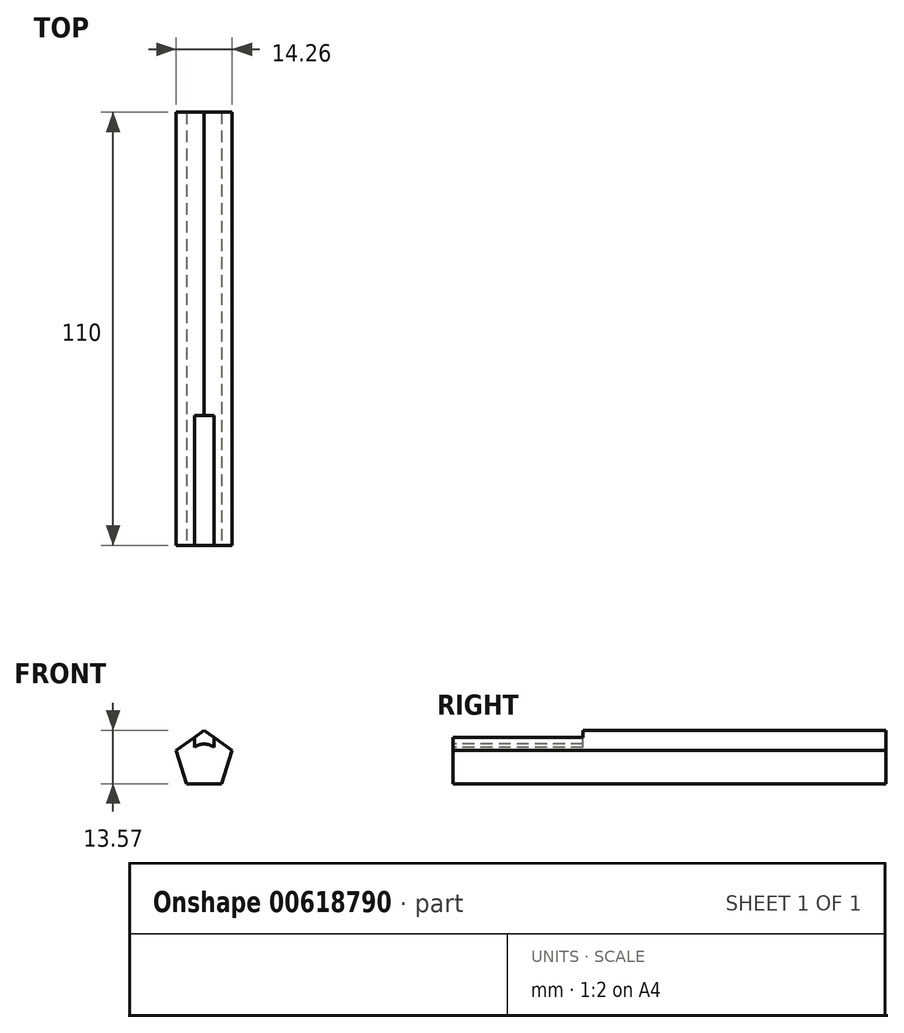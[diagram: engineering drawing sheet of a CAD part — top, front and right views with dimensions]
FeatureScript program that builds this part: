
annotation { "Feature Type Name" : "Feature", "Feature Type Description" : "" }
export const myFeature = defineFeature(function(context is Context, id is Id, definition is map)
    precondition{}
    {
        {
            var Q0;
            Q0=qCreatedBy(makeId("Front.planeOp"),FACE);
            var sketch = newSketch(context, id + "F0", { "sketchPlane" : qUnion([Q0])});
            skCircle(sketch, "E0", {"center": v(0, 0) * mm, "radius": 7.5 * mm});
            skCircle(sketch, "E1", {"center": v(0, 0) * mm, "radius": 1.5 * mm});
            skCircle(sketch, "E2", {"center": v(0, 0) * mm, "radius": 4 * mm});
            skCircle(sketch, "E3", {"center": v(0, 0) * mm, "radius": 5 * mm});
            skCircle(sketch, "E4.cCircle", {"center": v(0, 0) * mm, "radius": 7.5 * mm, "construction": true});
            skLineSegment(sketch, "E4.0", {"start": v(4.4, -6.07) * mm, "end": v(-4.4, -6.07) * mm});
            skLineSegment(sketch, "E4.1", {"start": v(-4.4, -6.07) * mm, "end": v(-7.13, 2.32) * mm});
            skLineSegment(sketch, "E4.2", {"start": v(-7.13, 2.32) * mm, "end": v(0, 7.5) * mm});
            skLineSegment(sketch, "E4.3", {"start": v(0, 7.5) * mm, "end": v(7.13, 2.32) * mm});
            skLineSegment(sketch, "E4.4", {"start": v(7.13, 2.32) * mm, "end": v(4.4, -6.07) * mm});
            skSolve(sketch);
        }
        {
            var Q0;
            Q0=qCreatedBy(makeId("Right.planeOp"),FACE);
            var sketch = newSketch(context, id + "F1", { "sketchPlane" : qUnion([Q0])});
            skLineSegment(sketch, "E5", {"start": v(0, 0) * mm, "end": v(95, 0) * mm});
            skLineSegment(sketch, "E6", {"start": v(0, 0) * mm, "end": v(0, 5.5) * mm});
            skLineSegment(sketch, "E7", {"start": v(0, 5.5) * mm, "end": v(95, 5.5) * mm});
            skLineSegment(sketch, "E8", {"start": v(95, 0) * mm, "end": v(110, 0) * mm});
            skLineSegment(sketch, "E9", {"start": v(0, 0) * mm, "end": v(0, 4) * mm});
            skLineSegment(sketch, "E10", {"start": v(0, 4) * mm, "end": v(95, 4) * mm});
            skLineSegment(sketch, "E11", {"start": v(95, 4) * mm, "end": v(110, 1.5) * mm});
            skLineSegment(sketch, "E12", {"start": v(110, 1.5) * mm, "end": v(110, 0) * mm});
            skLineSegment(sketch, "E13", {"start": v(95, 5.5) * mm, "end": v(110, 5.5) * mm});
            skLineSegment(sketch, "E14", {"start": v(110, 5.5) * mm, "end": v(110, 1.5) * mm});
            skSolve(sketch);
        }
        {
            var Q0;
            Q0=makeQuery(id+"F1.imprint","IMPRINT",FACE,{"disambiguationData":[TD([[makeQuery(id+"F1.imprint","IMPRINT",EDGE,{"derivedFrom":sQuery(id+"F1.wireOp",EDGE,"E6")}),-1.0]])]});
            var Q1;
            Q1=sQuery(id+"F1.wireOp",EDGE,"E5");
            revolve(context, id + "F2", {"entities" : qUnion([Q0]), "axis" : qUnion([Q1]), "revolveType" : RevolveType.FULL});
        }
        {
            var Q0;
            Q0=makeQuery(id+"F0.imprint","IMPRINT",FACE,{"disambiguationData":[TD([[makeQuery(id+"F0.imprint","IMPRINT",EDGE,{"derivedFrom":sQuery(id+"F0.wireOp",EDGE,"E3")}),-1.0]])]});
            extrude(context, id + "F3", {"entities" : qUnion([Q0]), "operationType" : NewBodyOperationType.ADD, "oppositeDirection" : true, "depth" : 110 * mm, "offsetDistance" : 25 * mm});
        }
        {
            var Q0;
            Q0=makeQuery(id+"F3.boolean.opBoolean","MERGE",FACE,{"derivedFrom":[makeQuery(id+"F2.opRevolve","SWEPT_FACE",FACE,{"disambiguationData":[OSD([sQuery(id+"F1.wireOp",EDGE,"E6")])]}),makeQuery(id+"F3.opExtrude","CAP_FACE",FACE,{"disambiguationData":[OSD([sQuery(id+"F0.wireOp",EDGE,"E3"),sQuery(id+"F0.wireOp",EDGE,"E4.0"),sQuery(id+"F0.wireOp",EDGE,"E4.1"),sQuery(id+"F0.wireOp",EDGE,"E4.2"),sQuery(id+"F0.wireOp",EDGE,"E4.3"),sQuery(id+"F0.wireOp",EDGE,"E4.4")])],"isStart":true})]});
            var sketch = newSketch(context, id + "F4", { "sketchPlane" : qUnion([Q0])});
            skCircle(sketch, "E15", {"center": v(0, 0) * mm, "radius": 4 * mm});
            skLineSegment(sketch, "E16", {"start": v(0, 0) * mm, "end": v(4, 0) * mm});
            skLineSegment(sketch, "E17", {"start": v(0, 0) * mm, "end": v(0, 10) * mm});
            skLineSegment(sketch, "E18", {"start": v(2.5, 0) * mm, "end": v(2.5, 10) * mm});
            skLineSegment(sketch, "E19", {"start": v(-2.5, 0) * mm, "end": v(-2.5, 10) * mm});
            skLineSegment(sketch, "E20", {"start": v(-2.5, 0) * mm, "end": v(0, 0) * mm});
            skLineSegment(sketch, "E21", {"start": v(-2.5, 10) * mm, "end": v(0, 10) * mm});
            skLineSegment(sketch, "E22", {"start": v(2.5, 10) * mm, "end": v(0, 10) * mm});
            skSolve(sketch);
        }
        {
            var Q0;
            {var subQ0=sQuery(id+"F4.wireOp",EDGE,"E17");var subQ1=sQuery(id+"F4.wireOp",EDGE,"E15");var subQ2=makeQuery(id+"F4.imprint","INTERSECT",VERTEX,{"derivedFrom":[subQ1,subQ0]});Q0=makeQuery(id+"F4.imprint","IMPRINT",FACE,{"disambiguationData":[TD([[makeQuery(id+"F4.imprint","IMPRINT",EDGE,{"disambiguationData":[TD([[subQ2,-1.0]])],"derivedFrom":subQ1}),-1.0]])]});}
            var Q1;
            {var subQ0=sQuery(id+"F4.wireOp",EDGE,"E18");var subQ1=sQuery(id+"F4.wireOp",EDGE,"E15");var subQ2=makeQuery(id+"F4.imprint","INTERSECT",VERTEX,{"derivedFrom":[subQ1,subQ0]});Q1=makeQuery(id+"F4.imprint","IMPRINT",FACE,{"disambiguationData":[TD([[makeQuery(id+"F4.imprint","IMPRINT",EDGE,{"disambiguationData":[TD([[subQ2,-1.0]])],"derivedFrom":subQ1}),-1.0]])]});}
            extrude(context, id + "F5", {"entities" : qUnion([Q0, Q1]), "operationType" : NewBodyOperationType.REMOVE, "oppositeDirection" : true, "depth" : 33 * mm, "offsetDistance" : 25 * mm});
        }
    });
